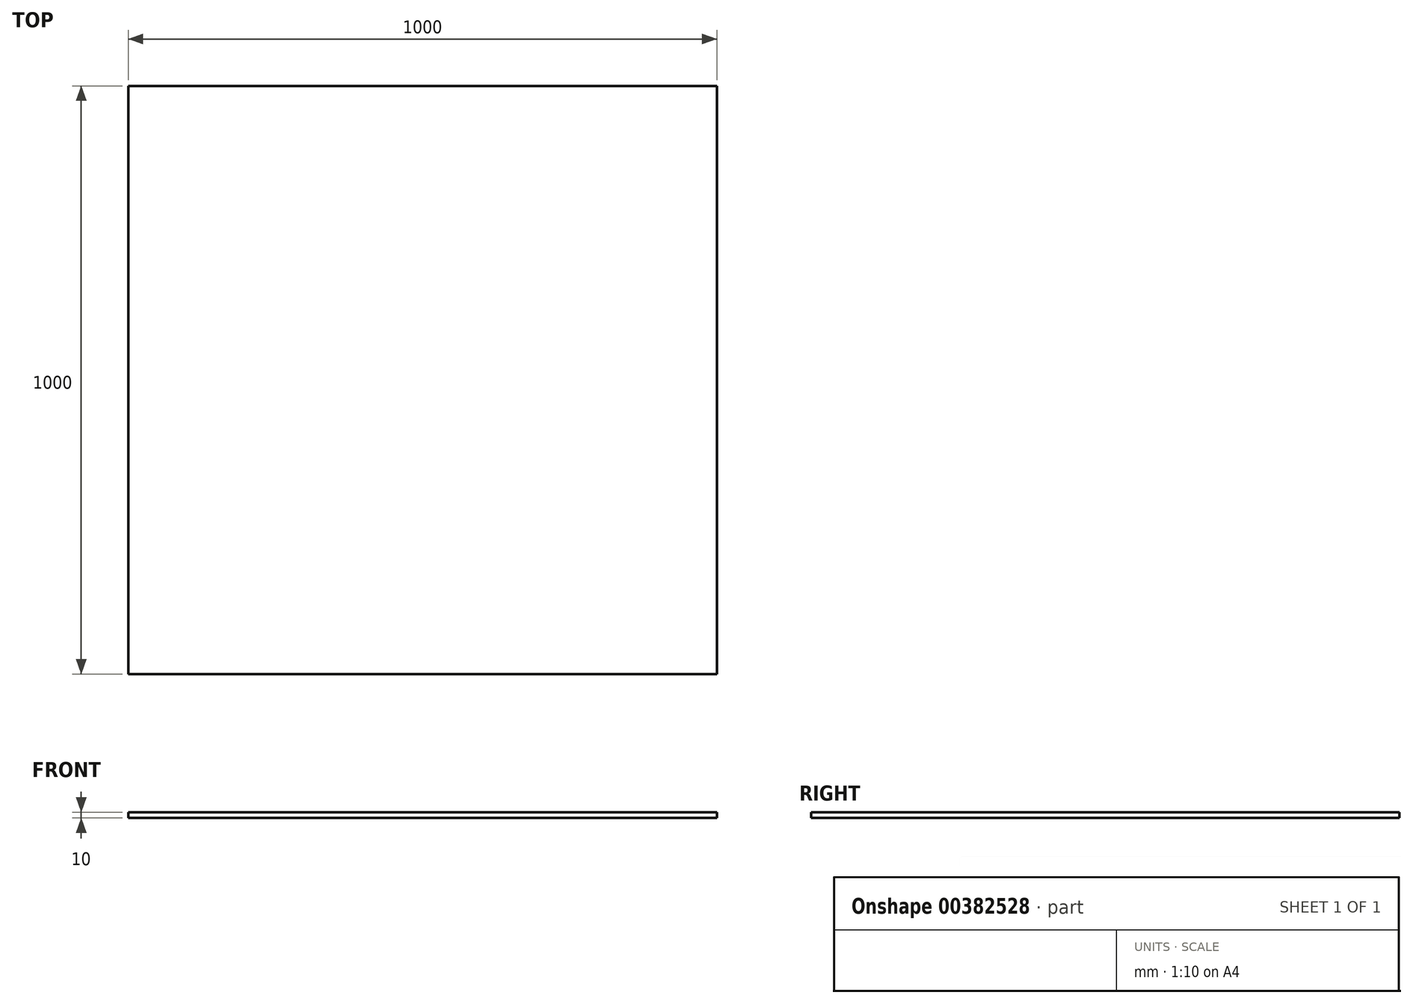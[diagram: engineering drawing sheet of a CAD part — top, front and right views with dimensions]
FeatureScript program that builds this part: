
annotation { "Feature Type Name" : "Feature", "Feature Type Description" : "" }
export const myFeature = defineFeature(function(context is Context, id is Id, definition is map)
    precondition{}
    {
        {
            var Q0;
            Q0=qCreatedBy(makeId("Top.planeOp"),FACE);
            var sketch = newSketch(context, id + "F0", { "sketchPlane" : qUnion([Q0])});
            skLineSegment(sketch, "E0.bottom", {"start": v(-500, 500) * mm, "end": v(500, 500) * mm});
            skLineSegment(sketch, "E0.top", {"start": v(-500, -500) * mm, "end": v(500, -500) * mm});
            skLineSegment(sketch, "E0.left", {"start": v(-500, 500) * mm, "end": v(-500, -500) * mm});
            skLineSegment(sketch, "E0.right", {"start": v(500, 500) * mm, "end": v(500, -500) * mm});
            skLineSegment(sketch, "E1", {"start": v(-500, 500) * mm, "end": v(500, -500) * mm});
            skPoint(sketch, "E2", {"position": v(0, 0) * mm});
            skSolve(sketch);
        }
        {
            var Q0;
            Q0=makeQuery(id+"F0.imprint","IMPRINT",FACE,{"disambiguationData":[TD([[makeQuery(id+"F0.imprint","IMPRINT",EDGE,{"derivedFrom":sQuery(id+"F0.wireOp",EDGE,"E0.top")}),1.0]])]});
            var Q1;
            Q1=makeQuery(id+"F0.imprint","IMPRINT",FACE,{"disambiguationData":[TD([[makeQuery(id+"F0.imprint","IMPRINT",EDGE,{"derivedFrom":sQuery(id+"F0.wireOp",EDGE,"E0.bottom")}),-1.0]])]});
            extrude(context, id + "F1", {"entities" : qUnion([Q0, Q1]), "depth" : 10 * mm});
        }
    });
